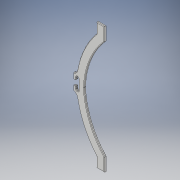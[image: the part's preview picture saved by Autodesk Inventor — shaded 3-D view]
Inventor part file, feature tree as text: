
AUTODESK INVENTOR PART (.ipt)
format: ipt  version: 2018 (Build 220112000, 112)  size: 236,544 bytes
history: native  units: mm
features: extrude x2, fillet x2, sketch x2, mirror x1
ambient origin geometry x8: Origin, YZ Plane, XZ Plane, XY Plane, X Axis, Y Axis, Z Axis, Center Point
bodies: Volumenkörper1 (feature_tree)
feature tree (7):
  extrude  "Extrusion1"  Depth=15.0mm
  mirror  "Spiegeln1"
  extrude  "Extrusion2"  TaperAngle=0.0deg  [1 undecoded]
  fillet  "Rundung1"  Radius=120.0mm
  fillet  "Rundung2"  Radius=150.0mm
  sketch  "Skizze1"  dims[d0=25.0mm d2=15.0mm]
  sketch  "Skizze2"  dims[d4=54.0mm d5=0.0mm d6=120.0mm d7=150.0mm d9=5.0mm d10=15.0mm d11=15.0mm d12=4.0mm d13=0.0mm d15=10.0mm d16=5.0mm d17=10.0mm d18=5.0mm d19=5.0mm d20=24.0mm d21=4.5mm d22=4.0mm d23=0.0mm d24=10.0mm d25=1.0mm]
note: 1 required parameter value undecoded (feature->parameter linkage not recoverable at this tier; creation-order binding heuristic only, values carry confidence <= 0.55)
